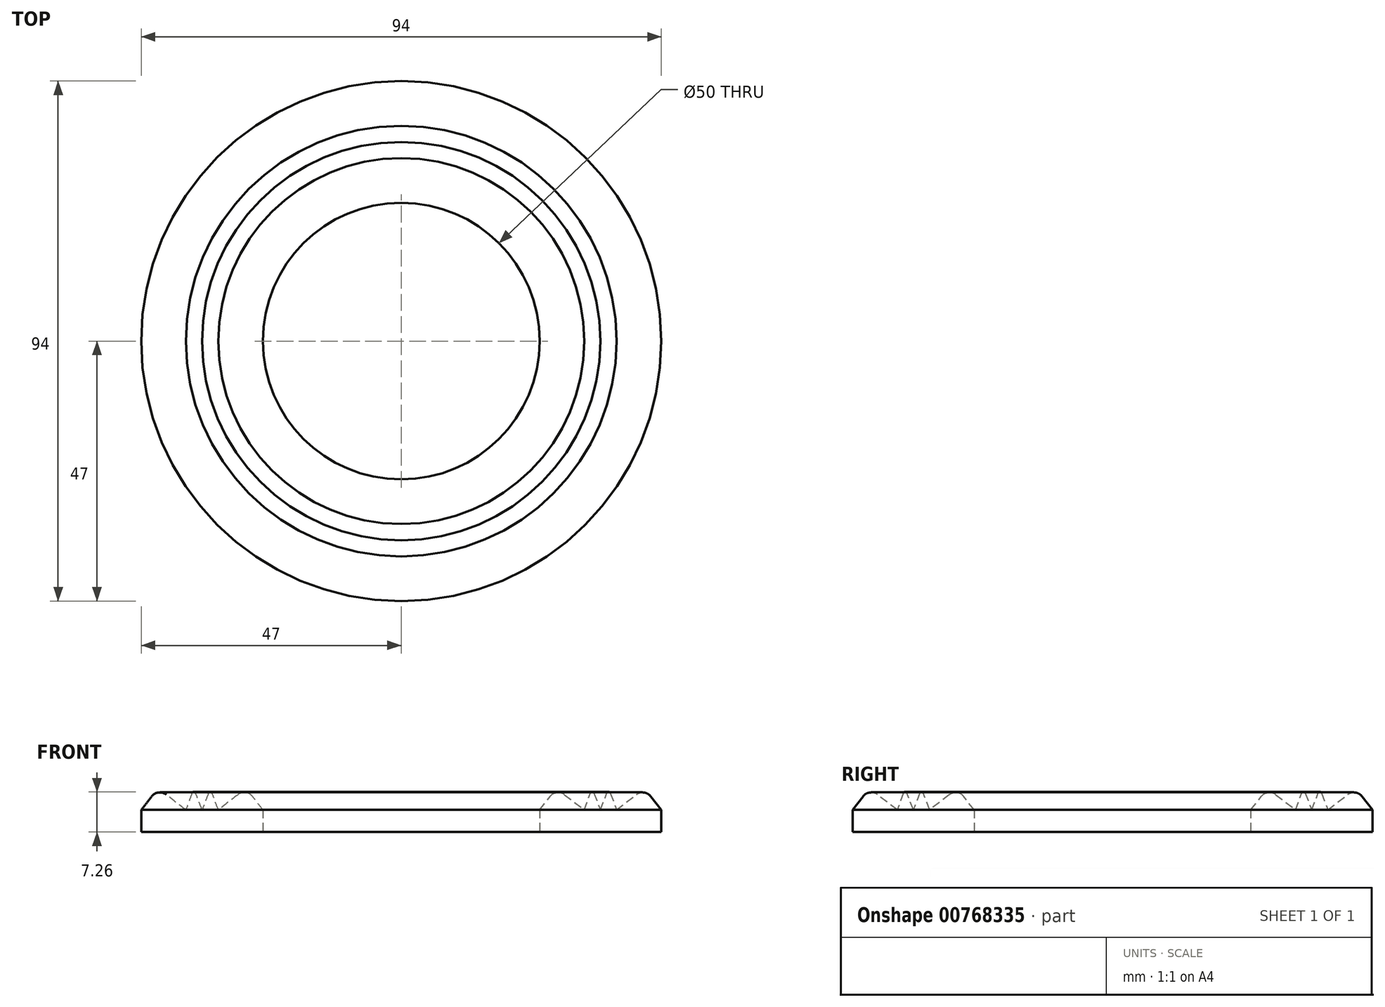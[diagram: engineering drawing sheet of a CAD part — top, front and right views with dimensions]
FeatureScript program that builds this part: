
annotation { "Feature Type Name" : "Feature", "Feature Type Description" : "" }
export const myFeature = defineFeature(function(context is Context, id is Id, definition is map)
    precondition{}
    {
        {
            var Q0;
            Q0=qCreatedBy(makeId("Front.planeOp"),FACE);
            var sketch = newSketch(context, id + "F0", { "sketchPlane" : qUnion([Q0])});
            skLineSegment(sketch, "E0", {"start": v(-25, 0) * mm, "end": v(-47, 0) * mm});
            skLineSegment(sketch, "E1", {"start": v(-47, 0) * mm, "end": v(-47, 4) * mm});
            skLineSegment(sketch, "E2", {"start": v(-33.07, 4) * mm, "end": v(-33.05, 4) * mm});
            skLineSegment(sketch, "E3", {"start": v(-25, 4) * mm, "end": v(-25, 0) * mm});
            skLineSegment(sketch, "E4", {"start": v(0, 0) * mm, "end": v(0, 4) * mm});
            skLineSegment(sketch, "E5", {"start": v(-47, 4) * mm, "end": v(-45.1, 6.45) * mm});
            skLineSegment(sketch, "E6", {"start": v(-42.5, 6.78) * mm, "end": v(-38.93, 4) * mm});
            skLineSegment(sketch, "E7", {"start": v(-33.07, 3.98) * mm, "end": v(-33.02, 4.04) * mm});
            skLineSegment(sketch, "E8", {"start": v(-25.02, 4) * mm, "end": v(-25, 3.98) * mm});
            skPoint(sketch, "E9.start.orphan", {"position": v(-47, 2) * mm});
            skLineSegment(sketch, "E10.MirrorCS", {"start": v(-29.5, 6.78) * mm, "end": v(-33.07, 4) * mm});
            skLineSegment(sketch, "E11.MirrorCS", {"start": v(-25, 4) * mm, "end": v(-26.9, 6.45) * mm});
            skLineSegment(sketch, "E12", {"start": v(-38.93, 4) * mm, "end": v(-37.82, 7.03) * mm});
            skLineSegment(sketch, "E13", {"start": v(-37.17, 7.04) * mm, "end": v(-36, 4) * mm});
            skLineSegment(sketch, "E14.MirrorCS", {"start": v(-34.83, 7.04) * mm, "end": v(-36, 4) * mm});
            skLineSegment(sketch, "E15.MirrorCS", {"start": v(-33.07, 4) * mm, "end": v(-34.18, 7.03) * mm});
            skPoint(sketch, "E16.end.orphan", {"position": v(-36, 0) * mm});
            skLineSegment(sketch, "E17.trimOffspring", {"start": v(-25.02, 4) * mm, "end": v(-25, 4) * mm});
            skPoint(sketch, "E18.visualSharp", {"position": v(-43.96, 7.91) * mm});
            skArc(sketch, "E18.filletArc", {"start": v(-42.5, 6.78) * mm, "mid": v(-43.86, 7.15) * mm, "end": v(-45.1, 6.45) * mm});
            skPoint(sketch, "E19.visualSharp", {"position": v(-28.04, 7.91) * mm});
            skArc(sketch, "E19.filletArc", {"start": v(-26.9, 6.45) * mm, "mid": v(-28.14, 7.15) * mm, "end": v(-29.5, 6.78) * mm});
            skPoint(sketch, "E20.visualSharp", {"position": v(-37.5, 7.91) * mm});
            skArc(sketch, "E20.filletArc", {"start": v(-37.17, 7.04) * mm, "mid": v(-37.5, 7.26) * mm, "end": v(-37.82, 7.03) * mm});
            skArc(sketch, "E21.MirrorCS", {"start": v(-34.83, 7.04) * mm, "mid": v(-34.5, 7.26) * mm, "end": v(-34.18, 7.03) * mm});
            skSolve(sketch);
        }
        {
            var Q0;
            Q0 = qSketchRegion(id + "F0", true);
            var Q1;
            Q1=sQuery(id+"F0.wireOp",EDGE,"E4");
            revolve(context, id + "F1", {"surfaceOperationType" : NewSurfaceOperationType.NEW, "entities" : qUnion([Q0]), "axis" : qUnion([Q1]), "revolveType" : RevolveType.FULL});
        }
    });
